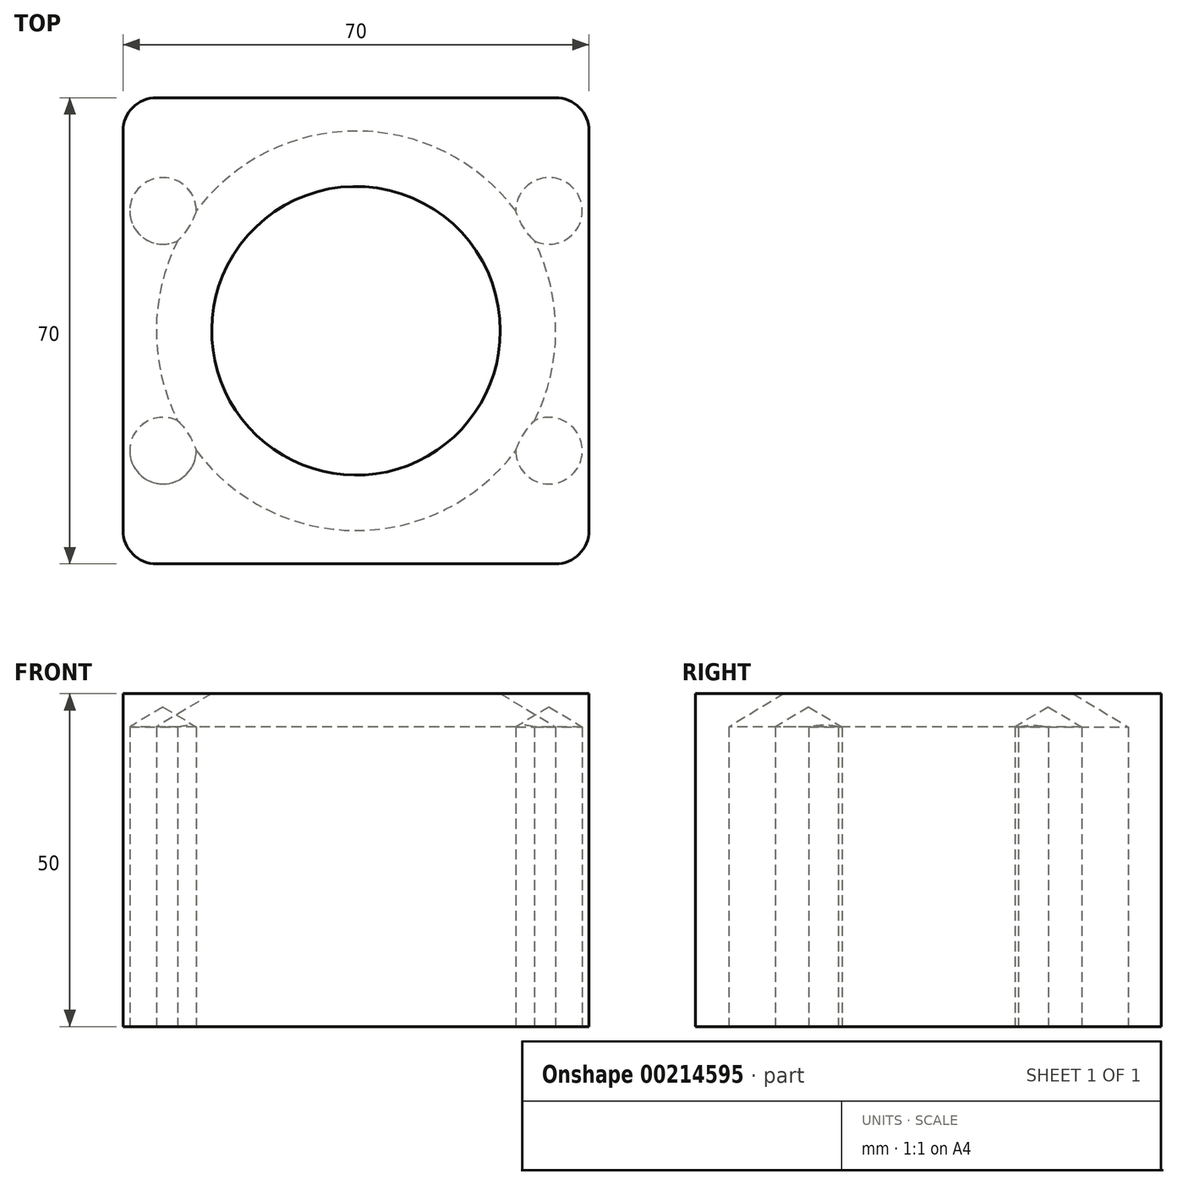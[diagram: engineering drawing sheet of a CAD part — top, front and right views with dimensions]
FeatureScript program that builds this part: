
annotation { "Feature Type Name" : "Feature", "Feature Type Description" : "" }
export const myFeature = defineFeature(function(context is Context, id is Id, definition is map)
    precondition{}
    {
        {
            var Q0;
            Q0=qCreatedBy(makeId("Top.planeOp"),FACE);
            var sketch = newSketch(context, id + "F0", { "sketchPlane" : qUnion([Q0])});
            skLineSegment(sketch, "E0.bottom", {"start": v(0, 0) * mm, "end": v(-70, 0) * mm});
            skLineSegment(sketch, "E0.top", {"start": v(0, 70) * mm, "end": v(-70, 70) * mm});
            skLineSegment(sketch, "E0.left", {"start": v(0, 0) * mm, "end": v(0, 70) * mm});
            skLineSegment(sketch, "E0.right", {"start": v(-70, 0) * mm, "end": v(-70, 70) * mm});
            skCircle(sketch, "E1", {"center": v(-35, 35) * mm, "radius": 20 * mm});
            skSolve(sketch);
        }
        {
            var Q0;
            Q0=makeQuery(id+"F0.imprint","IMPRINT",FACE,{"disambiguationData":[TD([[makeQuery(id+"F0.imprint","IMPRINT",EDGE,{"derivedFrom":sQuery(id+"F0.wireOp",EDGE,"E0.bottom")}),-1.0]])]});
            var sketch = newSketch(context, id + "F1", { "sketchPlane" : qUnion([Q0])});
            skPoint(sketch, "E2", {"position": v(-64, 17) * mm});
            skPoint(sketch, "E3", {"position": v(-6, 17) * mm});
            skPoint(sketch, "E4", {"position": v(-6, 53) * mm});
            skPoint(sketch, "E5", {"position": v(-64, 53) * mm});
            skSolve(sketch);
        }
        {
            var Q0;
            Q0=makeQuery(id+"F0.imprint","IMPRINT",FACE,{"disambiguationData":[TD([[makeQuery(id+"F0.imprint","IMPRINT",EDGE,{"derivedFrom":sQuery(id+"F0.wireOp",EDGE,"E0.bottom")}),-1.0]])]});
            var sketch = newSketch(context, id + "F2", { "sketchPlane" : qUnion([Q0])});
            skCircle(sketch, "E6", {"center": v(-64, 53) * mm, "radius": 5 * mm});
            skCircle(sketch, "E7", {"center": v(-64, 17) * mm, "radius": 5 * mm});
            skCircle(sketch, "E8", {"center": v(-6, 17) * mm, "radius": 5 * mm});
            skCircle(sketch, "E9", {"center": v(-6, 53) * mm, "radius": 5 * mm});
            skSolve(sketch);
        }
        {
            var Q0;
            Q0=makeQuery(id+"F0.imprint","IMPRINT",FACE,{"disambiguationData":[TD([[makeQuery(id+"F0.imprint","IMPRINT",EDGE,{"derivedFrom":sQuery(id+"F0.wireOp",EDGE,"E0.bottom")}),-1.0]])]});
            extrude(context, id + "F3", {"entities" : qUnion([Q0]), "depth" : 50 * mm});
        }
        {
            var Q0;
            Q0=sQuery(id+"F1.wireOp",VERTEX,"E2");
            var Q1;
            Q1=makeQuery(id+"F3.opExtrude","SWEPT_BODY",BODY,{"disambiguationData":[OSD([sQuery(id+"F0.wireOp",EDGE,"E0.bottom"),sQuery(id+"F0.wireOp",EDGE,"E0.top"),sQuery(id+"F0.wireOp",EDGE,"E0.left"),sQuery(id+"F0.wireOp",EDGE,"E0.right"),sQuery(id+"F0.wireOp",EDGE,"E1")])]});
            hole(context, id + "F4", {"style" : HoleStyle.SIMPLE, "endStyle" : HoleEndStyle.BLIND, "oppositeDirection" : true, "holeDiameter" : 10 * mm, "holeDepth" : 45 * mm, "locations" : qUnion([Q0]), "scope" : qUnion([Q1])});
        }
        {
            var Q0;
            Q0=sQuery(id+"F2.wireOp",VERTEX,"E9.center");
            var Q1;
            Q1=sQuery(id+"F2.wireOp",VERTEX,"E8.center");
            var Q2;
            Q2=sQuery(id+"F2.wireOp",VERTEX,"E6.center");
            var Q3;
            Q3=makeQuery(id+"F3.opExtrude","SWEPT_BODY",BODY,{"disambiguationData":[OSD([sQuery(id+"F0.wireOp",EDGE,"E0.bottom"),sQuery(id+"F0.wireOp",EDGE,"E0.top"),sQuery(id+"F0.wireOp",EDGE,"E0.left"),sQuery(id+"F0.wireOp",EDGE,"E0.right"),sQuery(id+"F0.wireOp",EDGE,"E1")])]});
            hole(context, id + "F5", {"style" : HoleStyle.SIMPLE, "endStyle" : HoleEndStyle.BLIND, "oppositeDirection" : true, "holeDiameter" : 10 * mm, "holeDepth" : 45 * mm, "locations" : qUnion([Q0, Q1, Q2]), "scope" : qUnion([Q3])});
        }
        {
            var Q0;
            Q0=makeQuery(id+"F3.opExtrude","CAP_FACE",FACE,{"disambiguationData":[OSD([sQuery(id+"F0.wireOp",EDGE,"E0.bottom"),sQuery(id+"F0.wireOp",EDGE,"E0.top"),sQuery(id+"F0.wireOp",EDGE,"E0.left"),sQuery(id+"F0.wireOp",EDGE,"E0.right"),sQuery(id+"F0.wireOp",EDGE,"E1")])],"isStart":true});
            var sketch = newSketch(context, id + "F6", { "sketchPlane" : qUnion([Q0])});
            skCircle(sketch, "E10", {"center": v(-35, -35) * mm, "radius": 30 * mm});
            skSolve(sketch);
        }
        {
            var Q0;
            Q0=makeQuery(id+"F3.opExtrude","SWEPT_EDGE",EDGE,{"disambiguationData":[OSD([sQuery(id+"F0.wireOp",EDGE,"E0.bottom"),sQuery(id+"F0.wireOp",EDGE,"E0.left")])]});
            fillet(context, id + "F7", {"entities" : qUnion([Q0]), "radius" : 5 * mm, "tangentPropagation" : true, "allowEdgeOverflow" : false});
        }
        {
            var Q0;
            Q0=makeQuery(id+"F3.opExtrude","SWEPT_EDGE",EDGE,{"disambiguationData":[OSD([sQuery(id+"F0.wireOp",EDGE,"E0.bottom"),sQuery(id+"F0.wireOp",EDGE,"E0.right")])]});
            fillet(context, id + "F8", {"entities" : qUnion([Q0]), "radius" : 5 * mm, "tangentPropagation" : true, "allowEdgeOverflow" : false});
        }
        {
            var Q0;
            Q0=makeQuery(id+"F3.opExtrude","SWEPT_EDGE",EDGE,{"disambiguationData":[OSD([sQuery(id+"F0.wireOp",EDGE,"E0.top"),sQuery(id+"F0.wireOp",EDGE,"E0.left")])]});
            fillet(context, id + "F9", {"entities" : qUnion([Q0]), "radius" : 5 * mm, "tangentPropagation" : true, "allowEdgeOverflow" : false});
        }
        {
            var Q0;
            Q0=makeQuery(id+"F3.opExtrude","SWEPT_EDGE",EDGE,{"disambiguationData":[OSD([sQuery(id+"F0.wireOp",EDGE,"E0.top"),sQuery(id+"F0.wireOp",EDGE,"E0.right")])]});
            fillet(context, id + "F10", {"entities" : qUnion([Q0]), "radius" : 5 * mm, "tangentPropagation" : true, "allowEdgeOverflow" : false});
        }
        {
            var Q0;
            Q0=sQuery(id+"F6.wireOp",VERTEX,"E10.center");
            var Q1;
            Q1=makeQuery(id+"F3.opExtrude","SWEPT_BODY",BODY,{"disambiguationData":[OSD([sQuery(id+"F0.wireOp",EDGE,"E0.bottom"),sQuery(id+"F0.wireOp",EDGE,"E0.top"),sQuery(id+"F0.wireOp",EDGE,"E0.left"),sQuery(id+"F0.wireOp",EDGE,"E0.right"),sQuery(id+"F0.wireOp",EDGE,"E1")])]});
            hole(context, id + "F11", {"style" : HoleStyle.SIMPLE, "endStyle" : HoleEndStyle.BLIND, "holeDiameter" : 60 * mm, "holeDepth" : 45 * mm, "startFromSketch" : true, "locations" : qUnion([Q0]), "scope" : qUnion([Q1])});
        }
    });
